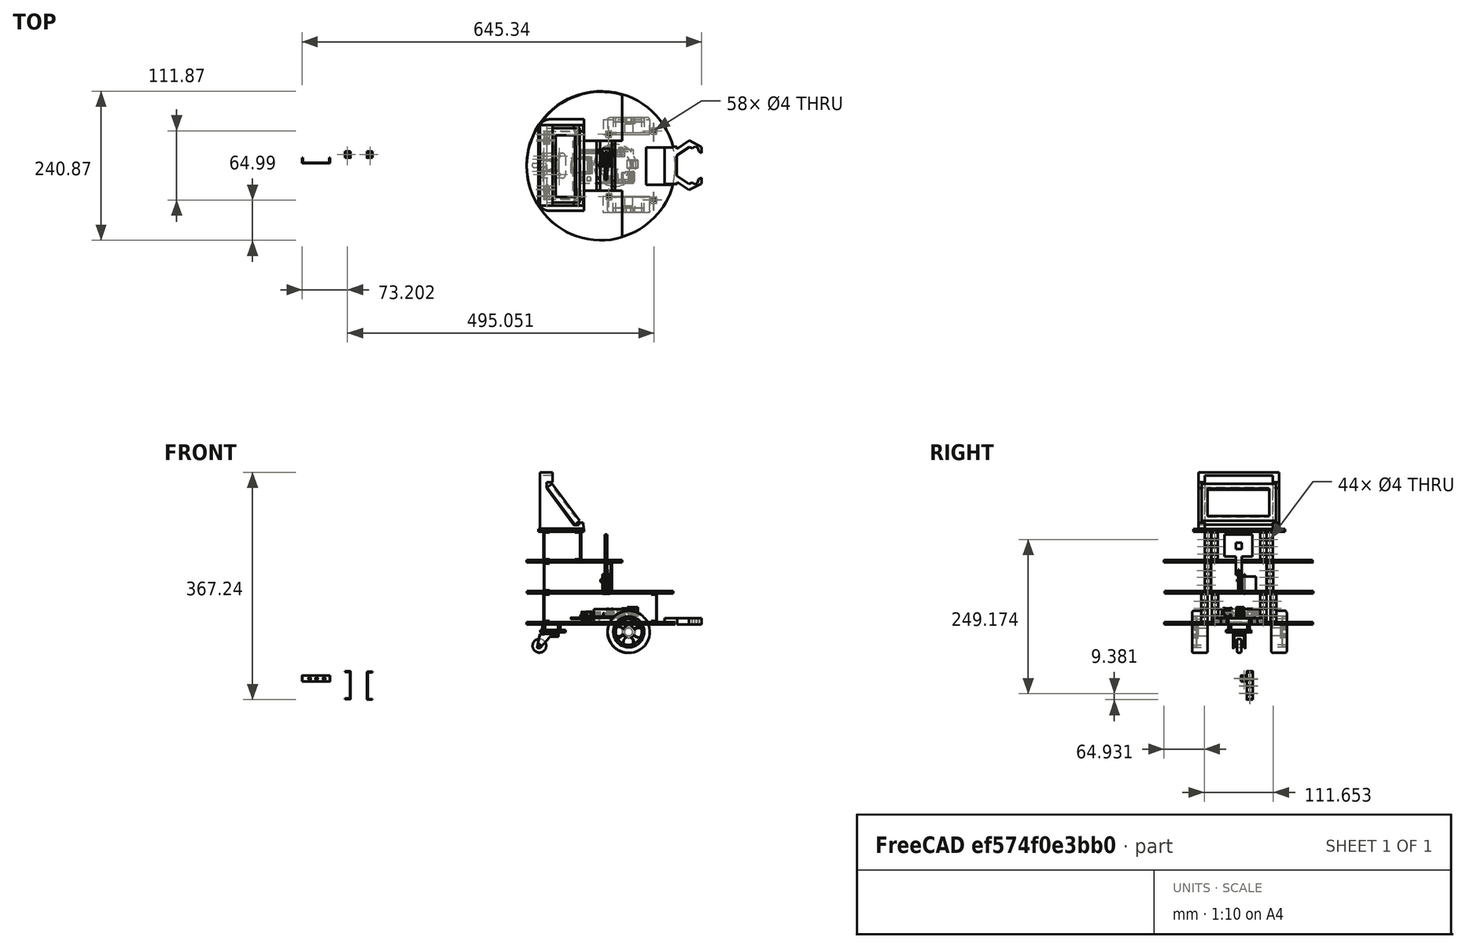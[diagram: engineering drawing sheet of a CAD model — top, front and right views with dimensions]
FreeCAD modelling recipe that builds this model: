
FCSTD DOCUMENT
Label: robot
objects: Part::Feature×53, Part::Cylinder×29, Part::Cut×29, Sketcher::SketchObject×12, PartDesign::Pad×11, App::DocumentObjectGroup×11, Part::MultiFuse×7, Part::Box×7, Part::Fillet×3, Mesh::Feature×1
note: 162 computed .brp shape members not serialized (recipe doc carries the construction recipe); baked Part::Feature solids carry a one-line shape summary decoded from their .brp

FEATURE [Sketcher::SketchObject] Sketch
  sketch-geometry (25):
    g0: LineSegment StartX=6.49 StartY=27.5 StartZ=0 EndX=26.49 EndY=27.5 EndZ=0
    g1: LineSegment StartX=26.49 StartY=27.5 StartZ=0 EndX=26.49 EndY=22.5 EndZ=0
    g2: LineSegment StartX=6.49 StartY=22.5 StartZ=0 EndX=6.49 EndY=27.5 EndZ=0
    g3: Circle CenterX=-114.698 CenterY=15.0203 CenterZ=0 NormalX=0 NormalY=0 NormalZ=1 Radius=2
    g4: Circle CenterX=-114.727 CenterY=-14.9797 CenterZ=0 NormalX=0 NormalY=0 NormalZ=1 Radius=2
    g5: Circle CenterX=-89.6981 CenterY=14.9764 CenterZ=0 NormalX=0 NormalY=0 NormalZ=1 Radius=2
    g6: Circle CenterX=-89.7274 CenterY=-14.9847 CenterZ=0 NormalX=0 NormalY=0 NormalZ=1 Radius=2
    g7: Circle CenterX=-109.963 CenterY=-38.9599 CenterZ=0 NormalX=0 NormalY=0 NormalZ=1 Radius=2
    g8: Circle CenterX=-109.887 CenterY=38.9911 CenterZ=0 NormalX=0 NormalY=0 NormalZ=1 Radius=2
    g9: Circle CenterX=61.9576 CenterY=55.4728 CenterZ=0 NormalX=0 NormalY=0 NormalZ=1 Radius=2
    g10: Circle CenterX=61.8489 CenterY=-55.7773 CenterZ=0 NormalX=0 NormalY=0 NormalZ=1 Radius=2
    g11: LineSegment StartX=56.3229 StartY=50 StartZ=0 EndX=56.3229 EndY=73.8727 EndZ=0
    g12: Circle CenterX=-22.6039 CenterY=-0.518752 CenterZ=0 NormalX=0 NormalY=0 NormalZ=1 Radius=120.029
    g13: LineSegment StartX=-18.6122 StartY=73.8727 StartZ=0 EndX=-18.6122 EndY=50 EndZ=0
    g14: LineSegment StartX=-19.3379 StartY=-50 StartZ=0 EndX=-19.3379 EndY=-75.8206 EndZ=0
    g15: LineSegment StartX=-18.6122 StartY=50 StartZ=0 EndX=56.3229 EndY=50 EndZ=0
    g16: LineSegment StartX=-19.3379 StartY=-50 StartZ=0 EndX=56.3229 EndY=-50 EndZ=0
    g17: LineSegment StartX=56.3229 StartY=-50 StartZ=0 EndX=56.2415 EndY=-75.8206 EndZ=0
    g18: LineSegment StartX=6.49001 StartY=-27.3051 StartZ=0 EndX=27.2747 EndY=-27.3051 EndZ=0
    g19: LineSegment StartX=27.2747 StartY=-27.3051 StartZ=0 EndX=27.2747 EndY=-22.4338 EndZ=0
    g20: LineSegment StartX=6.49001 StartY=-27.3051 StartZ=0 EndX=6.49001 EndY=-22.4338 EndZ=0
    g21: LineSegment StartX=6.49001 StartY=-22.4338 StartZ=0 EndX=27.2747 EndY=-22.4338 EndZ=0
    g22: LineSegment StartX=6.49 StartY=22.5 StartZ=0 EndX=26.49 EndY=22.5 EndZ=0
    g23: LineSegment StartX=-18.6122 StartY=73.8727 StartZ=0 EndX=56.3229 EndY=73.8727 EndZ=0
    g24: LineSegment StartX=-19.3379 StartY=-75.8206 StartZ=0 EndX=56.2415 EndY=-75.8206 EndZ=0
  constraints (25):
    c: Coincident(g0,g1)
    c: Coincident(g2,g0)
    c: Symmetric(g10,g9,g3)
    c: Coincident(g15,g13)
    c: Coincident(g15,g11)
    c: Coincident(g16,g14)
    c: Coincident(g17,g16)
    c: Horizontal(g18)
    c: Coincident(g19,g18)
    c: Vertical(g19)
    c: Coincident(g20,g18)
    c: Vertical(g20)
    c: Coincident(g21,g20)
    c: Coincident(g21,g19)
    c: Horizontal(g21)
    c: Coincident(g22,g2)
    c: Coincident(g22,g1)
    c: Horizontal(g22)
    c: Coincident(g23,g13)
    c: Coincident(g23,g11)
    c: Horizontal(g23)
    c: Coincident(g24,g14)
    c: Coincident(g24,g17)
    c: Horizontal(g24)
    c: Vertical(g14)
FEATURE [Sketcher::SketchObject] Sketch001
  sketch-geometry (25):
    g0: LineSegment [constr] StartX=-124.152 StartY=0.737365 StartZ=0 EndX=-29.7416 EndY=-0.0108822 EndZ=0
    g1: Circle CenterX=-110.299 CenterY=39.0839 CenterZ=0 NormalX=0 NormalY=0 NormalZ=1 Radius=2
    g2: Circle CenterX=-109.764 CenterY=-33.224 CenterZ=0 NormalX=0 NormalY=0 NormalZ=1 Radius=2
    g3: Circle CenterX=62.7977 CenterY=55.4219 CenterZ=0 NormalX=0 NormalY=0 NormalZ=1 Radius=2
    g4: Circle CenterX=62.9826 CenterY=-55.9466 CenterZ=0 NormalX=0 NormalY=0 NormalZ=1 Radius=2
    g5: LineSegment StartX=77.3278 StartY=28.8309 StartZ=0 EndX=50.3934 EndY=28.8309 EndZ=0
    g6: LineSegment StartX=50.3934 StartY=28.8309 StartZ=0 EndX=50.3934 EndY=-31.224 EndZ=0
    g7: Circle CenterX=-110.405 CenterY=-49.217 CenterZ=0 NormalX=0 NormalY=0 NormalZ=1 Radius=2
    g8: Circle CenterX=-109.615 CenterY=50.4676 CenterZ=0 NormalX=0 NormalY=0 NormalZ=1 Radius=2
    g9: Circle CenterX=-10.1147 CenterY=50.2419 CenterZ=0 NormalX=0 NormalY=0 NormalZ=1 Radius=2
    g10: Circle CenterX=-10.1344 CenterY=-50.6043 CenterZ=0 NormalX=0 NormalY=0 NormalZ=1 Radius=2
    g11: LineSegment StartX=-29.7491 StartY=40.2702 StartZ=0 EndX=-23.9444 EndY=40.2702 EndZ=0
    g12: LineSegment StartX=-23.9444 StartY=40.2702 StartZ=0 EndX=-23.9444 EndY=-40.2702 EndZ=0
    g13: LineSegment StartX=-23.9444 StartY=-40.2702 StartZ=0 EndX=-29.7491 EndY=-40.2702 EndZ=0
    g14: LineSegment StartX=-29.7491 StartY=-40.2702 StartZ=0 EndX=-29.7491 EndY=40.2702 EndZ=0
    g15: LineSegment StartX=-5.12768 StartY=40.2702 StartZ=0 EndX=0.362807 EndY=40.2702 EndZ=0
    g16: LineSegment StartX=0.362807 StartY=40.2702 StartZ=0 EndX=0.362807 EndY=-40.2701 EndZ=0
    g17: LineSegment StartX=0.362807 StartY=-40.2701 StartZ=0 EndX=-5.0695 EndY=-40.2701 EndZ=0
    g18: LineSegment StartX=-5.0695 StartY=-40.2701 StartZ=0 EndX=-5.12768 EndY=40.2702 EndZ=0
    g19: LineSegment [constr] StartX=-21.6534 StartY=-0.0749855 StartZ=0 EndX=-5.09844 EndY=-0.206192 EndZ=0
    g20: LineSegment [constr] StartX=50.3934 StartY=-0.645993 StartZ=0 EndX=76.3848 EndY=-0.851987 EndZ=0
    g21: LineSegment StartX=78.2127 StartY=-31.224 StartZ=0 EndX=50.3934 EndY=-31.224 EndZ=0
    g22: ArcOfCircle CenterX=-22.1678 CenterY=-0.347577 CenterZ=0 NormalX=0 NormalY=0 NormalZ=1 Radius=120 StartAngle=0.245617 EndAngle=6.02295
    g23: LineSegment StartX=77.3278 StartY=28.8309 StartZ=0 EndX=94.2307 EndY=28.8309 EndZ=0
    g24: LineSegment StartX=78.2127 StartY=-31.224 StartZ=0 EndX=93.7919 EndY=-31.224 EndZ=0
  constraints (36):
    c: Equal(g2,g1)
    c: Equal(g1,g3)
    c: Equal(g3,g4)
    c: Radius(g2) = 2
    c: Horizontal(g5)
    c: Coincident(g5,g6)
    c: Vertical(g6)
    c: Equal(g7,g8)
    c: Radius(g7) = 2
    c: Radius(g9) = 2
    c: Coincident(g11,g12)
    c: Coincident(g12,g13)
    c: Coincident(g13,g14)
    c: Coincident(g14,g11)
    c: Horizontal(g11)
    c: Horizontal(g13)
    c: Coincident(g15,g16)
    c: Coincident(g16,g17)
    c: Coincident(g17,g18)
    c: Coincident(g18,g15)
    c: Horizontal(g15)
    c: Horizontal(g17)
    c: Symmetric(g7,g8,g3)
    c: Tangent(g0,g19)
    c: PointOnObject(g20,g6)
    c: Tangent(g19,g20)
    c: PointOnObject(g19,g18)
    c: Coincident(g21,g6)
    c: Horizontal(g21)
    c: Radius(g22) = 120
    c: Coincident(g23,g5)
    c: Horizontal(g23)
    c: Horizontal(g24)
    c: Tangent(g24,g2)
    c: Coincident(g22,g23)
    c: Coincident(g22,g24)
FEATURE [PartDesign::Pad] Pad001
  Length = 4
  MirroredExtent = false
  Placement = pos=(0,0,50) rot=(0,0,1;0rad)
  Sketch = -> Sketch001
FEATURE [Sketcher::SketchObject] Sketch002
  sketch-geometry (14):
    g0: Circle CenterX=-109.932 CenterY=49.3917 CenterZ=0 NormalX=0 NormalY=0 NormalZ=1 Radius=2
    g1: Circle CenterX=-110.012 CenterY=-50.1232 CenterZ=0 NormalX=0 NormalY=0 NormalZ=1 Radius=2
    g2: Circle CenterX=-9.94777 CenterY=50.1271 CenterZ=0 NormalX=0 NormalY=0 NormalZ=1 Radius=2
    g3: Circle CenterX=-10.198 CenterY=-50.2781 CenterZ=0 NormalX=0 NormalY=0 NormalZ=1 Radius=2
    g4: LineSegment StartX=-67.9878 StartY=-40.9294 StartZ=0 EndX=-67.9878 EndY=39.6614 EndZ=0
    g5: Circle CenterX=-109.839 CenterY=41.6614 CenterZ=0 NormalX=0 NormalY=0 NormalZ=1 Radius=2
    g6: Circle CenterX=-110.415 CenterY=-38.9294 CenterZ=0 NormalX=0 NormalY=0 NormalZ=1 Radius=2
    g7: Circle CenterX=-59.5193 CenterY=-50.2572 CenterZ=0 NormalX=0 NormalY=0 NormalZ=1 Radius=2
    g8: Circle CenterX=-60.2629 CenterY=49.9665 CenterZ=0 NormalX=0 NormalY=0 NormalZ=1 Radius=2
    g9: ArcOfCircle CenterX=-22.4312 CenterY=-1.22279 CenterZ=0 NormalX=0 NormalY=0 NormalZ=1 Radius=120 StartAngle=1.28265 EndAngle=5.00053
    g10: LineSegment StartX=11.6694 StartY=113.83 StartZ=0 EndX=11.6694 EndY=39.6614 EndZ=0
    g11: LineSegment StartX=-67.9878 StartY=39.6614 StartZ=0 EndX=11.6694 EndY=39.6614 EndZ=0
    g12: LineSegment StartX=-67.9878 StartY=-40.9294 StartZ=0 EndX=11.6694 EndY=-40.9294 EndZ=0
    g13: LineSegment StartX=11.6694 StartY=-40.9294 StartZ=0 EndX=11.6694 EndY=-116.276 EndZ=0
  constraints (22):
    c: Equal(g0,g1)
    c: Equal(g1,g3)
    c: Equal(g3,g2)
    c: Radius(g0) = 2
    c: Vertical(g4)
    c: Equal(g6,g5)
    c: Equal(g5,g8)
    c: Equal(g8,g7)
    c: Radius(g6) = 2
    c: Radius(g9) = 120
    c: Vertical(g10)
    c: Coincident(g9,g10)
    c: Coincident(g9,g13)
    c: Coincident(g11,g4)
    c: Horizontal(g11)
    c: Tangent(g11,g5)
    c: Coincident(g12,g4)
    c: Horizontal(g12)
    c: Tangent(g12,g6)
    c: Coincident(g10,g11)
    c: Coincident(g13,g12)
    c: Tangent(g10,g13)
FEATURE [PartDesign::Pad] Pad002
  Length = 4
  MirroredExtent = false
  Placement = pos=(0,0,100) rot=(0,0,1;0rad)
  Sketch = -> Sketch002
FEATURE [Sketcher::SketchObject] Sketch003
  sketch-geometry (12):
    g0: ArcOfCircle CenterX=-105.074 CenterY=55.6821 CenterZ=0 NormalX=0 NormalY=0 NormalZ=1 Radius=18.6332 StartAngle=1.60655 EndAngle=3.14159
    g1: ArcOfCircle CenterX=-105.346 CenterY=-55.3418 CenterZ=0 NormalX=0 NormalY=0 NormalZ=1 Radius=18.3958 StartAngle=3.20271 EndAngle=4.69093
    g2: LineSegment StartX=-50.0043 StartY=74.3033 StartZ=0 EndX=-50.0043 EndY=-73.7333 EndZ=0
    g3: LineSegment StartX=-105.74 StartY=74.3033 StartZ=0 EndX=-50.0043 EndY=74.3033 EndZ=0
    g4: LineSegment StartX=-105.741 StartY=-73.7333 StartZ=0 EndX=-50.0043 EndY=-73.7333 EndZ=0
    g5: Circle CenterX=-109.743 CenterY=39.5908 CenterZ=0 NormalX=0 NormalY=0 NormalZ=1 Radius=2
    g6: Circle CenterX=-110.279 CenterY=-40.0459 CenterZ=0 NormalX=0 NormalY=0 NormalZ=1 Radius=2
    g7: Circle CenterX=-60.203 CenterY=49.9128 CenterZ=0 NormalX=0 NormalY=0 NormalZ=1 Radius=2
    g8: Circle CenterX=-59.3002 CenterY=-50.3702 CenterZ=0 NormalX=0 NormalY=0 NormalZ=1 Radius=2
    g9: Circle CenterX=-116.132 CenterY=9.74953 CenterZ=0 NormalX=0 NormalY=0 NormalZ=1 Radius=2
    g10: Circle CenterX=-116.544 CenterY=-9.66085 CenterZ=0 NormalX=0 NormalY=0 NormalZ=1 Radius=2
    g11: LineSegment StartX=-123.707 StartY=55.6821 StartZ=0 EndX=-123.707 EndY=-56.4655 EndZ=0
  constraints (17):
    c: Coincident(g3,g0)
    c: Coincident(g3,g2)
    c: Coincident(g4,g1)
    c: Coincident(g4,g2)
    c: Equal(g6,g5)
    c: Equal(g5,g7)
    c: Equal(g7,g8)
    c: Radius(g6) = 2
    c: Horizontal(g3)
    c: Vertical(g2)
    c: Horizontal(g4)
    c: Equal(g10,g9)
    c: Radius(g9) = 2
    c: Coincident(g11,g0)
    c: Coincident(g11,g1)
    c: Vertical(g11)
    c: Tangent(g11,g0)
FEATURE [PartDesign::Pad] Pad003
  Length = 4
  MirroredExtent = false
  Placement = pos=(0,0,150) rot=(0,0,1;0rad)
  Sketch = -> Sketch003
FEATURE [Part::Cylinder] Cylinder005
  Angle = 360
  Height = 25
  Radius = 6.5
FEATURE [Part::Cylinder] Cylinder006
  Angle = 360
  Height = 10
  Radius = 10
FEATURE [Part::Cylinder] Cylinder010
  Angle = 360
  Height = 7
  Placement = pos=(0.664718,-16.3626,0) rot=(0,0,1;0rad)
  Radius = 8
FEATURE [Part::Cylinder] Cylinder011
  Angle = 360
  Height = 7
  Placement = pos=(16.4955,0.685902,0) rot=(0,0,1;0rad)
  Radius = 8
FEATURE [Part::Cylinder] Cylinder012
  Angle = 360
  Height = 7
  Placement = pos=(-16.3838,-1.44516,0) rot=(0,0,1;0rad)
  Radius = 8
FEATURE [Part::Cylinder] Cylinder013
  Angle = 360
  Height = 25
  Radius = 25
FEATURE [Part::Cylinder] Cylinder009
  Angle = 360
  Height = 7
  Placement = pos=(-0.248596,16.2122,0) rot=(0,0,1;0rad)
  Radius = 8
FEATURE [Part::MultiFuse] Fusion
  Placement = pos=(22,77,-12) rot=(1,0,0;1.5708rad)
  Shapes = -> [Cylinder006,Cylinder011,Cylinder012,Cylinder010,Cylinder009,Cylinder005]
FEATURE [Part::Cylinder] Cylinder014
  Angle = 360
  Height = 25
  Radius = 34
FEATURE [Part::Cylinder] Cylinder015
  Angle = 360
  Height = 25
  Radius = 21
FEATURE [Part::Cylinder] Cylinder016
  Angle = 360
  Height = 25
  Radius = 25
FEATURE [Part::Cut] Cut002
  Base = -> Cylinder016
  Placement = pos=(22,77,-12) rot=(1,0,0;1.5708rad)
  Tool = -> Cylinder015
FEATURE [Part::Fillet] Fillet
  Edges = 2 edges r=3: [Edge2,Edge3]
  Placement = pos=(22,77,-12) rot=(1,0,0;1.5708rad)
FEATURE [App::DocumentObjectGroup] Group  label="wheel"
  Group = -> [Cut002,Fusion,Fillet]
FEATURE [Part::Cylinder] Cylinder
  Angle = 360
  Height = 7
  Radius = 11
FEATURE [Part::Cylinder] Cylinder017
  Angle = 360
  Height = 7
  Radius = 2.5
FEATURE [Part::Cut] Cut
  Base = -> Cylinder
  Tool = -> Cylinder017
FEATURE [Part::Fillet] Fillet001
  Base = -> Cut
  Edges = 4 edges r=2: [Edge1,Edge3,Edge4,Edge5]
  Placement = pos=(-122,-3.4,-34.5) rot=(0,0.707107,0.707107;3.14159rad)
FEATURE [App::DocumentObjectGroup] Group001  label="wheel0"
  Group = -> [Cylinder017,Cylinder,Fillet001]
FEATURE [Sketcher::SketchObject] Sketch004
  sketch-geometry (11):
    g0: LineSegment StartX=-39.5249 StartY=-0.0489382 StartZ=0 EndX=-9.52487 EndY=-0.0489382 EndZ=0
    g1: LineSegment StartX=-9.52487 StartY=-0.0489382 StartZ=0 EndX=-5.3256 EndY=-21.3647 EndZ=0
    g2: LineSegment StartX=-6.46484 StartY=-22.7502 StartZ=0 EndX=-9.08519 EndY=-22.7502 EndZ=0
    g3: LineSegment StartX=-10.2117 StartY=-22.2424 StartZ=0 EndX=-25.3922 EndY=-5.06478 EndZ=0
    g4: LineSegment StartX=-27.2038 StartY=-4.24812 StartZ=0 EndX=-38.567 EndY=-4.24812 EndZ=0
    g5: LineSegment StartX=-39.5249 StartY=-3.29027 StartZ=0 EndX=-39.5249 EndY=-0.0489382 EndZ=0
    g6: ArcOfCircle CenterX=-6.46484 CenterY=-21.5891 CenterZ=0 NormalX=0 NormalY=0 NormalZ=1 Radius=1.16114 StartAngle=4.71239 EndAngle=6.4777
    g7: ArcOfCircle CenterX=-9.08519 CenterY=-21.2469 CenterZ=0 NormalX=0 NormalY=0 NormalZ=1 Radius=1.50333 StartAngle=3.86535 EndAngle=4.71239
    g8: ArcOfCircle CenterX=-27.2038 CenterY=-6.66574 CenterZ=0 NormalX=0 NormalY=0 NormalZ=1 Radius=2.41762 StartAngle=0.723759 EndAngle=1.5708
    g9: Circle CenterX=-8.87657 CenterY=-18.7194 CenterZ=0 NormalX=0 NormalY=0 NormalZ=1 Radius=2
    g10: ArcOfCircle CenterX=-38.567 CenterY=-3.29027 CenterZ=0 NormalX=0 NormalY=0 NormalZ=1 Radius=0.95785 StartAngle=3.14159 EndAngle=4.71239
  constraints (16):
    c: Horizontal(g0)
    c: Distance(g0) = 30
    c: Coincident(g1,g0)
    c: Horizontal(g2)
    c: Horizontal(g4)
    c: Coincident(g5,g0)
    c: Vertical(g5)
    c: Tangent(g1,g6)
    c: Tangent(g2,g6)
    c: Tangent(g2,g7)
    c: Tangent(g3,g7)
    c: Tangent(g3,g8)
    c: Tangent(g4,g8)
    c: Radius(g9) = 2
    c: Tangent(g4,g10)
    c: Tangent(g5,g10)
FEATURE [PartDesign::Pad] Pad004
  Length = 20
  MirroredExtent = false
  Placement = pos=(40,27,-2) rot=(0,0,1;0rad)
  Sketch = -> Sketch004
FEATURE [Part::Box] Box
  Height = 16
  Length = 40
  Width = 25
FEATURE [Part::Cut] Cut003
  Base = -> Pad004
  Placement = pos=(-90.7,-8,-42.5) rot=(0,0.707107,0.707107;3.14159rad)
  Tool = -> Box
FEATURE [App::DocumentObjectGroup] Group002  label="wl"
  Group = -> [Cut003]
FEATURE [Part::Fillet] Fillet002
  Edges = 2 edges r=3: [Edge2,Edge3]
  Placement = pos=(22.3,-76,-12) rot=(0,0.707107,0.707107;3.14159rad)
FEATURE [Part::MultiFuse] Fusion001
  Placement = pos=(22.3,-76,-12) rot=(0,0.707107,0.707107;3.14159rad)
  Shapes = -> [Cylinder006,Cylinder011,Cylinder012,Cylinder010,Cylinder009,Cylinder005]
FEATURE [Part::Cut] Cut004
  Base = -> Cylinder016
  Placement = pos=(22.3,-76,-12) rot=(0,0.707107,0.707107;3.14159rad)
  Tool = -> Cylinder015
FEATURE [App::DocumentObjectGroup] Group003  label="wheel01"
  Group = -> [Cut004,Fusion001,Fillet002]
FEATURE [App::DocumentObjectGroup] Group004
FEATURE [Sketcher::SketchObject] Sketch005  label="Sketch_plate"
  sketch-geometry (12):
    g0: LineSegment StartX=-114.888 StartY=19.7983 StartZ=0 EndX=-85.6217 EndY=19.7983 EndZ=0
    g1: LineSegment StartX=-80.1008 StartY=14.2774 StartZ=0 EndX=-80.1008 EndY=-15.4701 EndZ=0
    g2: LineSegment StartX=-85.6217 StartY=-20.991 StartZ=0 EndX=-114.888 EndY=-20.991 EndZ=0
    g3: LineSegment StartX=-120.409 StartY=-15.4701 StartZ=0 EndX=-120.409 EndY=14.2774 EndZ=0
    g4: Circle CenterX=-115.076 CenterY=14.931 CenterZ=0 NormalX=0 NormalY=0 NormalZ=1 Radius=2
    g5: Circle CenterX=-115.258 CenterY=-14.9052 CenterZ=0 NormalX=0 NormalY=0 NormalZ=1 Radius=2
    g6: Circle CenterX=-90.0087 CenterY=14.931 CenterZ=0 NormalX=0 NormalY=0 NormalZ=1 Radius=2
    g7: Circle CenterX=-89.8897 CenterY=-14.9413 CenterZ=0 NormalX=0 NormalY=0 NormalZ=1 Radius=2
    g8: ArcOfCircle CenterX=-85.6217 CenterY=14.2774 CenterZ=0 NormalX=0 NormalY=0 NormalZ=1 Radius=5.52093 StartAngle=0 EndAngle=1.5708
    g9: ArcOfCircle CenterX=-85.6217 CenterY=-15.4701 CenterZ=0 NormalX=0 NormalY=0 NormalZ=1 Radius=5.52093 StartAngle=4.71239 EndAngle=6.28319
    g10: ArcOfCircle CenterX=-114.888 CenterY=14.2774 CenterZ=0 NormalX=0 NormalY=0 NormalZ=1 Radius=5.52093 StartAngle=1.5708 EndAngle=3.14159
    g11: ArcOfCircle CenterX=-114.888 CenterY=-15.4701 CenterZ=0 NormalX=0 NormalY=0 NormalZ=1 Radius=5.52093 StartAngle=3.14159 EndAngle=4.71239
  constraints (19):
    c: Horizontal(g0)
    c: Horizontal(g2)
    c: Vertical(g1)
    c: Vertical(g3)
    c: Equal(g4,g5)
    c: Equal(g5,g7)
    c: Equal(g7,g6)
    c: Radius(g6) = 2
    c: Tangent(g0,g8)
    c: Tangent(g1,g8)
    c: Tangent(g1,g9)
    c: Tangent(g2,g9)
    c: Tangent(g0,g10)
    c: Tangent(g3,g10)
    c: Tangent(g2,g11)
    c: Tangent(g3,g11)
    c: Equal(g11,g10)
    c: Equal(g10,g8)
    c: Equal(g8,g9)
FEATURE [PartDesign::Pad] Pad
  Length = 4
  MirroredExtent = false
  Sketch = -> Sketch
FEATURE [PartDesign::Pad] Pad005
  Length = 4
  MirroredExtent = false
  Placement = pos=(0,0,-13) rot=(0,0,1;0rad)
  Sketch = -> Sketch005
FEATURE [Part::Cylinder] Cylinder018
  Angle = 360
  Height = 4
  Placement = pos=(-107,0,-16) rot=(0,0,1;0rad)
  Radius = 7
FEATURE [Part::Cylinder] Cylinder019
  Angle = 360
  Height = 10
  Placement = pos=(-115.055,-14.9752,-9) rot=(0,0,1;0rad)
  Radius = 2
FEATURE [Part::Cylinder] Cylinder020
  Angle = 360
  Height = 10
  Placement = pos=(-90.0431,-15,-10) rot=(0,0,1;0rad)
  Radius = 2
FEATURE [Part::Cylinder] Cylinder021
  Angle = 360
  Height = 10
  Placement = pos=(-89.9511,14.932,-10) rot=(0,0,1;0rad)
  Radius = 2
FEATURE [Part::Cylinder] Cylinder022
  Angle = 360
  Height = 10
  Placement = pos=(-115.109,14.8885,-9) rot=(0,0,1;0rad)
  Radius = 2
FEATURE [Sketcher::SketchObject] Sketch006
  sketch-geometry (15):
    g0: LineSegment StartX=-29.9116 StartY=5.05926 StartZ=0 EndX=30.0884 EndY=5.05926 EndZ=0
    g1: LineSegment StartX=34.7894 StartY=0.358325 StartZ=0 EndX=34.7894 EndY=-0.239814 EndZ=0
    g2: LineSegment StartX=30.0884 StartY=-4.94074 StartZ=0 EndX=-29.9116 EndY=-4.94074 EndZ=0
    g3: LineSegment StartX=-34.6125 StartY=-0.239814 StartZ=0 EndX=-34.6125 EndY=0.358325 EndZ=0
    g4: ArcOfCircle CenterX=-29.9116 CenterY=0.358325 CenterZ=0 NormalX=0 NormalY=0 NormalZ=1 Radius=4.70093 StartAngle=1.5708 EndAngle=3.14159
    g5: ArcOfCircle CenterX=-29.9116 CenterY=-0.239814 CenterZ=0 NormalX=0 NormalY=0 NormalZ=1 Radius=4.70093 StartAngle=3.14159 EndAngle=4.71239
    g6: ArcOfCircle CenterX=30.0884 CenterY=0.358325 CenterZ=0 NormalX=0 NormalY=0 NormalZ=1 Radius=4.70093 StartAngle=0 EndAngle=1.5708
    g7: ArcOfCircle CenterX=30.0884 CenterY=-0.239814 CenterZ=0 NormalX=0 NormalY=0 NormalZ=1 Radius=4.70093 StartAngle=4.71239 EndAngle=6.28319
    g8: Circle CenterX=-29.9299 CenterY=0.0119776 CenterZ=0 NormalX=0 NormalY=0 NormalZ=1 Radius=2
    g9: Circle CenterX=-11.1706 CenterY=0.0385086 CenterZ=0 NormalX=0 NormalY=0 NormalZ=1 Radius=2
    g10: Circle CenterX=11.1127 CenterY=-0.0115485 CenterZ=0 NormalX=0 NormalY=0 NormalZ=1 Radius=2
    g11: Circle CenterX=0.0455946 CenterY=-0.112972 CenterZ=0 NormalX=0 NormalY=0 NormalZ=1 Radius=2
    g12: Circle CenterX=30.0576 CenterY=0.117842 CenterZ=0 NormalX=0 NormalY=0 NormalZ=1 Radius=2
    g13: LineSegment StartX=25.3875 StartY=-4.94074 StartZ=0 EndX=25.3875 EndY=5.05926 EndZ=0
    g14: LineSegment StartX=-25.2106 StartY=-4.94074 StartZ=0 EndX=-25.2106 EndY=5.05926 EndZ=0
  constraints (30):
    c: Horizontal(g0)
    c: Horizontal(g2)
    c: Vertical(g1)
    c: Vertical(g3)
    c: Tangent(g0,g4)
    c: Tangent(g3,g4)
    c: Tangent(g2,g5)
    c: Tangent(g3,g5)
    c: Tangent(g0,g6)
    c: Tangent(g1,g6)
    c: Tangent(g1,g7)
    c: Tangent(g2,g7)
    c: Equal(g4,g5)
    c: Equal(g5,g6)
    c: Equal(g6,g7)
    c: Distance(g2) = 60
    c: DistanceY(g0,g2) = -10
    c: Equal(g8,g9)
    c: Equal(g9,g10)
    c: Equal(g10,g11)
    c: Equal(g11,g12)
    c: Radius(g8) = 2
    c: PointOnObject(g13,g2)
    c: PointOnObject(g13,g0)
    c: Vertical(g13)
    c: Tangent(g13,g6)
    c: PointOnObject(g14,g2)
    c: PointOnObject(g14,g0)
    c: Vertical(g14)
    c: Tangent(g14,g4)
FEATURE [Sketcher::SketchObject] Sketch007
  sketch-geometry (12):
    g0: LineSegment StartX=20.5461 StartY=-1.20827 StartZ=0 EndX=-22.4155 EndY=-1.20827 EndZ=0
    g1: LineSegment StartX=-23.4007 StartY=7.77698 StartZ=0 EndX=-22.4007 EndY=7.77698 EndZ=0
    g2: LineSegment StartX=-22.4007 StartY=7.77698 StartZ=0 EndX=-22.4007 EndY=0.197829 EndZ=0
    g3: LineSegment StartX=21.5992 StartY=7.84487 StartZ=0 EndX=20.5992 EndY=7.84487 EndZ=0
    g4: LineSegment StartX=20.5992 StartY=7.84487 StartZ=0 EndX=20.5992 EndY=-0.149263 EndZ=0
    g5: LineSegment StartX=-22.0096 StartY=-0.193299 StartZ=0 EndX=20.5552 EndY=-0.193299 EndZ=0
    g6: LineSegment StartX=-23.4007 StartY=7.77698 StartZ=0 EndX=-23.4007 EndY=-0.223018 EndZ=0
    g7: LineSegment StartX=21.5992 StartY=7.84487 StartZ=0 EndX=21.5992 EndY=-0.155135 EndZ=0
    g8: ArcOfCircle CenterX=-22.4155 CenterY=-0.223018 CenterZ=0 NormalX=0 NormalY=0 NormalZ=1 Radius=0.985254 StartAngle=3.14159 EndAngle=4.71239
    g9: ArcOfCircle CenterX=20.5461 CenterY=-0.155135 CenterZ=0 NormalX=0 NormalY=0 NormalZ=1 Radius=1.05314 StartAngle=4.71239 EndAngle=6.28319
    g10: ArcOfCircle CenterX=20.5552 CenterY=-0.149263 CenterZ=0 NormalX=0 NormalY=0 NormalZ=1 Radius=0.044036 StartAngle=4.71239 EndAngle=6.28319
    g11: ArcOfCircle CenterX=-22.0096 CenterY=0.197829 CenterZ=0 NormalX=0 NormalY=0 NormalZ=1 Radius=0.391129 StartAngle=3.14159 EndAngle=4.71239
  constraints (25):
    c: Coincident(g2,g1)
    c: Vertical(g2)
    c: Coincident(g4,g3)
    c: Vertical(g4)
    c: Distance(g1) = 1
    c: Distance(g3) = 1
    c: Coincident(g6,g1)
    c: Vertical(g6)
    c: Coincident(g7,g3)
    c: Vertical(g7)
    c: Tangent(g0,g8)
    c: Tangent(g6,g8)
    c: Tangent(g0,g9)
    c: Tangent(g7,g9)
    c: Tangent(g4,g10)
    c: Tangent(g5,g10)
    c: Tangent(g2,g11)
    c: Tangent(g5,g11)
    c: Distance(g1,g3) = 43
    c: Distance(g3,g7) = 8
    c: Distance(g1,g6) = 8
    c: Horizontal(g5)
    c: Horizontal(g0)
    c: Horizontal(g1)
    c: Horizontal(g3)
FEATURE [PartDesign::Pad] Pad006
  Length = 10
  MirroredExtent = false
  Sketch = -> Sketch007
FEATURE [Part::Cylinder] Cylinder025
  Angle = 360
  Height = 2
  Placement = pos=(25,5.38,4.9) rot=(0.706319,-0.023027,0.707519;3.16911rad)
  Radius = 2
FEATURE [Part::Cylinder] Cylinder026
  Angle = 360
  Height = 2
  Placement = pos=(-26,5.29,4.9) rot=(0.706319,-0.023027,0.707519;3.16911rad)
  Radius = 2
FEATURE [Part::Cylinder] Cylinder027
  Angle = 360
  Height = 2
  Placement = pos=(12.2129,0,4.81114) rot=(1,0,0;1.5708rad)
  Radius = 2
FEATURE [Part::Cylinder] Cylinder028
  Angle = 360
  Height = 2
  Placement = pos=(-11.1555,-4.76837e-07,4.86401) rot=(1,0,0;1.5708rad)
  Radius = 2
FEATURE [Part::Cylinder] Cylinder029
  Angle = 360
  Height = 2
  Placement = pos=(-2.98023e-07,0,4.86401) rot=(1,0,0;1.5708rad)
  Radius = 2
FEATURE [Part::Cut] Cut005
  Base = -> Pad006
  Tool = -> Cylinder025
FEATURE [Part::Cut] Cut006
  Base = -> Cut005
  Tool = -> Cylinder027
FEATURE [Part::Cut] Cut007
  Base = -> Cut006
  Tool = -> Cylinder029
FEATURE [Part::Cut] Cut008
  Base = -> Cut007
  Tool = -> Cylinder028
FEATURE [Part::Cut] Cut009
  Base = -> Cut008
  Tool = -> Cylinder026
FEATURE [Part::MultiFuse] Fusion002  label="back_wheel"
  Shapes = -> [Fillet001,Pad005,Cylinder018,Cylinder019,Cylinder020,Cylinder021,Cylinder022,Cut003]
FEATURE [Part::Cylinder] Cylinder030
  Angle = 360
  Height = 10
  Placement = pos=(15.49,3.9,4.87) rot=(0,1,0;1.5708rad)
  Radius = 2
FEATURE [Part::Cylinder] Cylinder031
  Angle = 360
  Height = 10
  Placement = pos=(-28.4147,3.9,5.14) rot=(0,1,0;1.5708rad)
  Radius = 2
FEATURE [Part::Cut] Cut018
  Base = -> Cut009
  Tool = -> Cylinder031
FEATURE [Part::Cut] Cut019
  Base = -> Cut018
  Placement = pos=(-481.872,4.52656,-92.3721) rot=(0,0,1;0rad)
  Tool = -> Cylinder030
FEATURE [Part::Cut] Cut022
  Base = -> Cut018
  Placement = pos=(-428.168,12.2394,-99.0758) rot=(-0.57735,0.57735,0.57735;2.0944rad)
  Tool = -> Cylinder030
FEATURE [Part::Cut] Cut023
  Base = -> Cut018
  Placement = pos=(-399.312,22.2394,-99.8057) rot=(0.57735,0.57735,-0.57735;2.0944rad)
  Tool = -> Cylinder030
FEATURE [App::DocumentObjectGroup] Group005  label="junk"
  Group = -> [Sketch006,Group001,Group002,Group004,Cut008,Cut019,Cut022,Cut023,Cylinder014,Cylinder013]
FEATURE [Part::Cut] Cut024
  Base = -> Cut018
  Placement = pos=(-114,44,26) rot=(0.57735,0.57735,-0.57735;2.0944rad)
  Tool = -> Cylinder030
FEATURE [Part::Cut] Cut025
  Base = -> Cut018
  Placement = pos=(66.5,-61.1,26) rot=(0.57735,-0.57735,-0.57735;4.18879rad)
  Tool = -> Cylinder030
FEATURE [Part::Cut] Cut026
  Base = -> Cut018
  Placement = pos=(66.5,50.5,26) rot=(0.57735,-0.57735,-0.57735;4.18879rad)
  Tool = -> Cylinder030
FEATURE [Part::Cut] Cut027
  Base = -> Cut018
  Placement = pos=(-113.8,-33.8,26) rot=(0.57735,0.57735,-0.57735;2.0944rad)
  Tool = -> Cylinder030
FEATURE [Part::Cut] Cut028
  Base = -> Cut018
  Placement = pos=(-113.8,54.6,75.9572) rot=(0.57735,0.57735,-0.57735;2.0944rad)
  Tool = -> Cylinder030
FEATURE [Part::Cut] Cut029
  Base = -> Cut018
  Placement = pos=(-113.8,-45.5244,76) rot=(0.57735,0.57735,-0.57735;2.0944rad)
  Tool = -> Cylinder030
FEATURE [Part::Cut] Cut030
  Base = -> Cut018
  Placement = pos=(-6.72542,45.23,76) rot=(0.57735,-0.57735,-0.57735;4.18879rad)
  Tool = -> Cylinder030
FEATURE [Part::Cut] Cut031
  Base = -> Cut018
  Placement = pos=(-6.2,-55.7,76) rot=(0.57735,-0.57735,-0.57735;4.18879rad)
  Tool = -> Cylinder030
FEATURE [Part::Cut] Cut032
  Base = -> Cut018
  Placement = pos=(-56.7371,44.4421,126) rot=(0.57735,-0.57735,-0.57735;4.18879rad)
  Tool = -> Cylinder030
FEATURE [Part::Cut] Cut033
  Base = -> Cut018
  Placement = pos=(-55.7549,-55.4537,126) rot=(0.57735,-0.57735,-0.57735;4.18879rad)
  Tool = -> Cylinder030
FEATURE [Part::Cut] Cut034
  Base = -> Cut018
  Placement = pos=(-114.175,-34.5899,126) rot=(0.57735,0.57735,-0.57735;2.0944rad)
  Tool = -> Cylinder030
FEATURE [Part::Cut] Cut035
  Base = -> Cut018
  Placement = pos=(-113.675,44.2743,126) rot=(0.57735,0.57735,-0.57735;2.0944rad)
  Tool = -> Cylinder030
FEATURE [App::DocumentObjectGroup] Group006  label="flor0"
  Group = -> [Cut027,Cut026,Cut025,Cut024]
FEATURE [App::DocumentObjectGroup] Group007  label="flor1"
  Group = -> [Cut028,Cut029,Cut030,Cut031]
FEATURE [App::DocumentObjectGroup] Group008  label="flor2"
  Group = -> [Cut032,Cut033,Cut034,Cut035]
FEATURE [Sketcher::SketchObject] Sketch008  label="gropper"
  sketch-geometry (24):
    g0: LineSegment StartX=80.2034 StartY=30.1452 StartZ=0 EndX=100.11 EndY=30.1452 EndZ=0
    g1: LineSegment StartX=100.216 StartY=-30.1776 StartZ=0 EndX=80.2034 EndY=-30.1776 EndZ=0
    g2: LineSegment StartX=80.2034 StartY=-30.1776 StartZ=0 EndX=80.2034 EndY=30.1452 EndZ=0
    g3: LineSegment StartX=139.974 StartY=29.5055 StartZ=0 EndX=139.974 EndY=19.9512 EndZ=0
    g4: LineSegment StartX=139.709 StartY=-20.0089 StartZ=0 EndX=140.068 EndY=-29.5025 EndZ=0
    g5: LineSegment StartX=125.379 StartY=27.6382 StartZ=0 EndX=129.678 EndY=30.5041 EndZ=0
    g6: LineSegment StartX=129.678 StartY=30.5041 StartZ=0 EndX=134.515 EndY=27.6382 EndZ=0
    g7: LineSegment StartX=134.515 StartY=27.6382 StartZ=0 EndX=135.589 EndY=22.4435 EndZ=0
    g8: LineSegment StartX=135.589 StartY=22.4435 StartZ=0 EndX=139.974 EndY=19.9512 EndZ=0
    g9: LineSegment StartX=124.663 StartY=-27.7113 StartZ=0 EndX=128.962 EndY=-31.1146 EndZ=0
    g10: LineSegment StartX=128.962 StartY=-31.1146 StartZ=0 EndX=133.619 EndY=-28.4278 EndZ=0
    g11: LineSegment StartX=133.619 StartY=-28.4278 StartZ=0 EndX=135.052 EndY=-22.8749 EndZ=0
    g12: LineSegment StartX=135.052 StartY=-22.8749 StartZ=0 EndX=139.709 EndY=-20.0089 EndZ=0
    g13: LineSegment StartX=100.11 StartY=30.1452 StartZ=0 EndX=100.11 EndY=26.5496 EndZ=0
    g14: LineSegment StartX=100.149 StartY=16.1353 StartZ=0 EndX=100.149 EndY=-17.1102 EndZ=0
    g15: LineSegment StartX=100.216 StartY=-30.1776 StartZ=0 EndX=100.216 EndY=-26.8315 EndZ=0
    g16: LineSegment StartX=100.11 StartY=26.5496 StartZ=0 EndX=120.202 EndY=39.9887 EndZ=0
    g17: LineSegment StartX=120.269 StartY=29.7499 StartZ=0 EndX=100.149 EndY=16.1353 EndZ=0
    g18: LineSegment StartX=119.814 StartY=-30.0538 StartZ=0 EndX=100.149 EndY=-17.1102 EndZ=0
    g19: LineSegment StartX=100.216 StartY=-26.8315 StartZ=0 EndX=119.826 EndY=-39.8917 EndZ=0
    g20: LineSegment StartX=120.202 StartY=39.9887 StartZ=0 EndX=139.974 EndY=29.5055 EndZ=0
    g21: LineSegment StartX=120.269 StartY=29.7499 StartZ=0 EndX=125.379 EndY=27.6382 EndZ=0
    g22: LineSegment StartX=119.814 StartY=-30.0538 StartZ=0 EndX=124.663 EndY=-27.7113 EndZ=0
    g23: LineSegment StartX=119.826 StartY=-39.8917 StartZ=0 EndX=140.068 EndY=-29.5025 EndZ=0
  constraints (30):
    c: Coincident(g1,g2)
    c: Coincident(g2,g0)
    c: Horizontal(g0)
    c: Horizontal(g1)
    c: Vertical(g2)
    c: Coincident(g5,g6)
    c: Coincident(g6,g7)
    c: Coincident(g7,g8)
    c: Coincident(g8,g3)
    c: Coincident(g9,g10)
    c: Coincident(g10,g11)
    c: Coincident(g11,g12)
    c: Coincident(g12,g4)
    c: Coincident(g13,g0)
    c: Vertical(g13)
    c: Vertical(g14)
    c: Coincident(g15,g1)
    c: Vertical(g15)
    c: Coincident(g16,g13)
    c: Coincident(g17,g14)
    c: Coincident(g18,g14)
    c: Coincident(g19,g15)
    c: Coincident(g20,g16)
    c: Coincident(g20,g3)
    c: Coincident(g21,g17)
    c: Coincident(g21,g5)
    c: Coincident(g22,g18)
    c: Coincident(g22,g9)
    c: Coincident(g23,g19)
    c: Coincident(g23,g4)
FEATURE [PartDesign::Pad] Pad007  label="gripper"
  Length = 10
  MirroredExtent = false
  Sketch = -> Sketch008
FEATURE [Part::Box] Box001
  Height = 87
  Length = 80
  Placement = pos=(-50,26,251.5) rot=(0,1,0;3.14159rad)
  Width = 110
FEATURE [Sketcher::SketchObject] Sketch009
  sketch-geometry (11):
    g0: LineSegment StartX=-120.266 StartY=55.8702 StartZ=0 EndX=-120.266 EndY=-35.2585 EndZ=0
    g1: LineSegment StartX=-120.266 StartY=-35.2585 StartZ=0 EndX=-50.1957 EndY=-35.2585 EndZ=0
    g2: LineSegment StartX=-50.1957 StartY=-35.2585 StartZ=0 EndX=-50.319 EndY=-25.484 EndZ=0
    g3: LineSegment StartX=-50.319 StartY=-25.484 StartZ=0 EndX=-57.7715 EndY=-25.484 EndZ=0
    g4: LineSegment StartX=-65.5367 StartY=-29.5767 StartZ=0 EndX=-109.382 EndY=30.4233 EndZ=0
    g5: LineSegment StartX=-109.382 StartY=30.4233 StartZ=0 EndX=-109.382 EndY=39.9073 EndZ=0
    g6: LineSegment StartX=-109.382 StartY=39.9073 StartZ=0 EndX=-100.312 EndY=39.9073 EndZ=0
    g7: LineSegment StartX=-100.312 StartY=39.9073 StartZ=0 EndX=-100.312 EndY=55.8702 EndZ=0
    g8: LineSegment StartX=-100.312 StartY=55.8702 StartZ=0 EndX=-120.266 EndY=55.8702 EndZ=0
    g9: LineSegment StartX=-65.5367 StartY=-29.5767 StartZ=0 EndX=-57.7715 EndY=-29.5767 EndZ=0
    g10: LineSegment StartX=-57.7715 StartY=-29.5767 StartZ=0 EndX=-57.7715 EndY=-25.484 EndZ=0
  constraints (20):
    c: Vertical(g0)
    c: Coincident(g0,g1)
    c: Horizontal(g1)
    c: Coincident(g1,g2)
    c: Coincident(g2,g3)
    c: Coincident(g4,g5)
    c: Vertical(g5)
    c: Coincident(g5,g6)
    c: Horizontal(g6)
    c: Coincident(g6,g7)
    c: Vertical(g7)
    c: Coincident(g7,g8)
    c: Coincident(g8,g0)
    c: Horizontal(g8)
    c: DistanceY(g4) = 60
    c: Coincident(g9,g4)
    c: Horizontal(g9)
    c: Coincident(g10,g9)
    c: Coincident(g10,g3)
    c: Horizontal(g3)
FEATURE [PartDesign::Pad] Pad008
  Length = 130
  MirroredExtent = false
  Placement = pos=(-1.15663,146.081,200.7) rot=(1,0,0;1.5708rad)
  Sketch = -> Sketch009
FEATURE [Part::Cut] Cut036
  Base = -> Pad008
  Placement = pos=(0.470886,-81.3035,-10.7339) rot=(0,0,1;0rad)
  Tool = -> Box001
FEATURE [Sketcher::SketchObject] Sketch010
  sketch-geometry (4):
    g0: LineSegment StartX=-125.009 StartY=156.743 StartZ=0 EndX=-50.0091 EndY=156.743 EndZ=0
    g1: LineSegment StartX=-50.0091 StartY=156.743 StartZ=0 EndX=-50.0091 EndY=36.7431 EndZ=0
    g2: LineSegment StartX=-50.0091 StartY=36.7431 StartZ=0 EndX=-125.009 EndY=36.7431 EndZ=0
    g3: LineSegment StartX=-125.009 StartY=36.7431 StartZ=0 EndX=-125.009 EndY=156.743 EndZ=0
  constraints (10):
    c: Coincident(g0,g1)
    c: Coincident(g1,g2)
    c: Coincident(g2,g3)
    c: Coincident(g3,g0)
    c: Horizontal(g0)
    c: Horizontal(g2)
    c: Vertical(g1)
    c: Vertical(g3)
    c: DistanceY(g3) = 120
    c: DistanceX(g0) = 75
FEATURE [PartDesign::Pad] Pad009
  Length = 10
  MirroredExtent = false
  Sketch = -> Sketch010
FEATURE [Part::Box] Box002
  Height = 10
  Length = 55
  Placement = pos=(-115,45.8,7.5) rot=(0,0,1;0rad)
  Width = 100
FEATURE [Part::Cut] Cut037  label="display"
  Base = -> Pad009
  Placement = pos=(-34.7923,-97.0035,121.476) rot=(0,1,0;0.928855rad)
  Tool = -> Box002
FEATURE [Part::Box] Box003
  Height = 23
  Length = 23
  Placement = pos=(28.3401,28.6705,-9.64305) rot=(0,0,1;0rad)
  Width = 12
FEATURE [Part::Box] Box004
  Height = 1.7
  Length = 32
  Placement = pos=(24.15,28.6705,7.9668) rot=(0,0,1;0rad)
  Width = 12
FEATURE [Part::Cylinder] Cylinder032
  Angle = 360
  Height = 10
  Placement = pos=(53.8219,34.6,2.58368) rot=(0,0,1;0rad)
  Radius = 1
FEATURE [Part::Cylinder] Cylinder034
  Angle = 360
  Height = 10
  Placement = pos=(26.1112,34.5,1.79316) rot=(0,0,1;0rad)
  Radius = 1
FEATURE [Part::MultiFuse] Fusion003
  Shapes = -> [Box004,Box003]
FEATURE [Part::Cut] Cut038
  Base = -> Fusion003
  Tool = -> Cylinder034
FEATURE [Part::Cut] Cut039
  Base = -> Cut038
  Tool = -> Cylinder032
FEATURE [Part::Cylinder] Cylinder035
  Angle = 360
  Height = 10
  Placement = pos=(41.2515,34.4472,6.56) rot=(0,0,1;0rad)
  Radius = 2
FEATURE [Part::Cylinder] Cylinder036
  Angle = 360
  Height = 10
  Placement = pos=(34.4857,34.67,6.56) rot=(0,0,1;0rad)
  Radius = 6
FEATURE [Part::Box] Box005
  Height = 1.5
  Length = 37
  Width = 4.5
FEATURE [Part::Box] Box006
  Height = 1.5
  Length = 17
  Placement = pos=(20.2342,-6.49055,0) rot=(0,0,1;1.5708rad)
  Width = 4.5
FEATURE [Part::MultiFuse] Fusion004
  Placement = pos=(16.4876,32.0839,17.56) rot=(0,0,1;0rad)
  Shapes = -> [Box006,Box005]
FEATURE [Part::Cylinder] Cylinder037
  Angle = 360
  Height = 10
  Placement = pos=(34.5,34.5,10.7594) rot=(0,0,1;0rad)
  Radius = 2
FEATURE [Part::MultiFuse] Fusion005
  Placement = pos=(-49,17.44,105.53) rot=(0.57735,0.57735,-0.57735;2.0944rad)
  Shapes = -> [Cylinder035,Cylinder036,Cut039]
FEATURE [Part::MultiFuse] Fusion006
  Placement = pos=(-48.6,17.44,105.53) rot=(0.57735,0.57735,-0.57735;2.0944rad)
  Shapes = -> [Fusion004,Cylinder037]
FEATURE [Sketcher::SketchObject] Sketch011
  sketch-geometry (12):
    g0: LineSegment StartX=-95.0946 StartY=32.3618 StartZ=0 EndX=-60.0946 EndY=32.3618 EndZ=0
    g1: LineSegment StartX=-59.724 StartY=-12.6382 StartZ=0 EndX=-95.0946 EndY=-12.6382 EndZ=0
    g2: LineSegment StartX=-95.0946 StartY=-12.6382 StartZ=0 EndX=-95.0946 EndY=32.3618 EndZ=0
    g3: LineSegment StartX=-60.0946 StartY=15.2279 StartZ=0 EndX=-29.8289 EndY=15.2279 EndZ=0
    g4: LineSegment StartX=-29.8289 StartY=15.2279 StartZ=0 EndX=-29.8289 EndY=5.22794 EndZ=0
    g5: LineSegment StartX=-29.8289 StartY=5.22794 StartZ=0 EndX=-59.724 EndY=5.22794 EndZ=0
    g6: LineSegment StartX=-59.724 StartY=-12.6382 StartZ=0 EndX=-59.724 EndY=5.22794 EndZ=0
    g7: LineSegment StartX=-60.0946 StartY=15.2279 StartZ=0 EndX=-60.0946 EndY=32.3618 EndZ=0
    g8: LineSegment StartX=-82.1826 StartY=15.2164 StartZ=0 EndX=-72.1826 EndY=15.2164 EndZ=0
    g9: LineSegment StartX=-72.1826 StartY=15.2164 StartZ=0 EndX=-72.1826 EndY=5.21644 EndZ=0
    g10: LineSegment StartX=-72.1826 StartY=5.21644 StartZ=0 EndX=-82.1826 EndY=5.21644 EndZ=0
    g11: LineSegment StartX=-82.1826 StartY=5.21644 StartZ=0 EndX=-82.1826 EndY=15.2164 EndZ=0
  constraints (29):
    c: Coincident(g1,g2)
    c: Coincident(g2,g0)
    c: Horizontal(g0)
    c: Horizontal(g1)
    c: Vertical(g2)
    c: Coincident(g3,g4)
    c: Coincident(g4,g5)
    c: Horizontal(g3)
    c: Horizontal(g5)
    c: Vertical(g4)
    c: Coincident(g6,g1)
    c: Coincident(g6,g5)
    c: Vertical(g6)
    c: Coincident(g7,g3)
    c: Coincident(g7,g0)
    c: Vertical(g7)
    c: DistanceY(g4) = -10
    c: Coincident(g8,g9)
    c: Coincident(g9,g10)
    c: Coincident(g10,g11)
    c: Coincident(g11,g8)
    c: Horizontal(g8)
    c: Horizontal(g10)
    c: Vertical(g9)
    c: Vertical(g11)
    c: DistanceY(g2) = 45
    c: DistanceX(g0) = 35
    c: DistanceY(g9) = -10
    c: DistanceX(g8) = 10
FEATURE [PartDesign::Pad] Pad010  label="camera_Pad"
  Length = 4
  MirroredExtent = false
  Placement = pos=(-16.3,-10.67,50) rot=(0,1,0;1.5708rad)
  Sketch = -> Sketch011
FEATURE [App::DocumentObjectGroup] Group009  label="micro_servo"
  Group = -> [Fusion006,Fusion005,Pad010]
FEATURE [Part::Feature] RaspBerry
  Placement = pos=(-12.8029,-1.75778,11.0436) rot=(1,0,0;1.5708rad)
  shape: bbox 85.6 x 53.98 x 1.35 mm, 6 faces (baked)
FEATURE [Part::Feature] RaspBerry001
  Placement = pos=(-55.5029,-21.2478,13.6186) rot=(0.57735,-0.57735,-0.57735;2.0944rad)
  shape: bbox 5.461 x 7.999 x 2.949 mm, 809 faces (baked)
FEATURE [Part::Feature] RaspBerry002
  Placement = pos=(-50.8029,-21.2478,13.6186) rot=(0.57735,-0.57735,-0.57735;2.0944rad)
  shape: bbox 3.937 x 6.982 x 2.155 mm, 206 faces (baked)
FEATURE [Part::Feature] RaspBerry003 .. RaspBerry007  x5 (patterned run collapsed; names and placements below)
  shape: bbox 4 x 0.37 x 1.716 mm, 43 faces (baked)
  placements: all 5 at pos=(-50.8029,-21.2478,13.6186) rot=(0.57735,-0.57735,-0.57735;2.0944rad)
FEATURE [Part::Feature] RaspBerry008
  Placement = pos=(-11.3429,-29.2478,15.6986) rot=(1,0,0;1.5708rad)
  shape: bbox 15 x 12 x 8.275 mm, 506 faces (baked)
FEATURE [Part::Feature] RaspBerry009
  Placement = pos=(31.4971,-18.8103,18.9976) rot=(0.57735,0.57735,0.57735;2.0944rad)
  shape: bbox 20.57 x 17.91 x 14.48 mm, 219 faces (baked)
FEATURE [Part::Feature] RaspBerry010
  Placement = pos=(-55.0129,-0.297781,11.0436) rot=(0.57735,0.57735,-0.57735;4.18879rad)
  shape: bbox 3 x 0.7 x 1.3 mm, 115 faces (baked)
FEATURE [Part::Feature] RaspBerry011
  Placement = pos=(-55.0129,-0.297781,11.0436) rot=(0.57735,0.57735,-0.57735;4.18879rad)
  shape: bbox 32.12 x 24.12 x 2.1 mm, 97 faces (baked)
FEATURE [Part::Feature] RaspBerry012
  Placement = pos=(-55.0129,-0.297781,11.0436) rot=(0.57735,0.57735,-0.57735;4.18879rad)
  shape: bbox 4.8 x 1.9 x 0.1 mm, 6 faces (baked)
FEATURE [Part::Feature] RaspBerry013
  Placement = pos=(-55.0129,-0.297781,11.0436) rot=(0.57735,0.57735,-0.57735;4.18879rad)
  shape: bbox 4.8 x 1.9 x 0.1 mm, 6 faces (baked)
FEATURE [Part::Feature] RaspBerry014
  Placement = pos=(-55.0129,-0.297781,11.0436) rot=(0.57735,0.57735,-0.57735;4.18879rad)
  shape: bbox 5.9 x 1.9 x 0.1 mm, 6 faces (baked)
FEATURE [Part::Feature] RaspBerry015
  Placement = pos=(-55.0129,-0.297781,11.0436) rot=(0.57735,0.57735,-0.57735;4.18879rad)
  shape: bbox 5.9 x 1.9 x 0.1 mm, 6 faces (baked)
FEATURE [Part::Feature] RaspBerry016
  Placement = pos=(-55.0129,-0.297781,11.0436) rot=(0.57735,0.57735,-0.57735;4.18879rad)
  shape: bbox 4.8 x 1.9 x 0.1 mm, 6 faces (baked)
FEATURE [Part::Feature] RaspBerry017
  Placement = pos=(-55.0129,-0.297781,11.0436) rot=(0.57735,0.57735,-0.57735;4.18879rad)
  shape: bbox 4.8 x 1.9 x 0.1 mm, 6 faces (baked)
FEATURE [Part::Feature] RaspBerry018
  Placement = pos=(-55.0129,-0.297781,11.0436) rot=(0.57735,0.57735,-0.57735;4.18879rad)
  shape: bbox 4.8 x 3.6 x 0.1 mm, 10 faces (baked)
FEATURE [Part::Feature] RaspBerry019
  Placement = pos=(-55.0129,-0.297781,11.0436) rot=(0.57735,0.57735,-0.57735;4.18879rad)
  shape: bbox 6.819 x 1.9 x 0.1 mm, 9 faces (baked)
FEATURE [Part::Feature] RaspBerry020
  Placement = pos=(9.36709,22.2322,12.3936) rot=(0.57735,-0.57735,-0.57735;2.0944rad)
  shape: bbox 12 x 15 x 10.79 mm, 46 faces (baked)
FEATURE [Part::Feature] RaspBerry021 .. RaspBerry024  x4 (patterned run collapsed; names and placements below)
  shape: bbox 1.145 x 2 x 7.071 mm, 28 faces (baked)
  placements: all 4 at pos=(9.36709,22.2322,12.3936) rot=(0.57735,-0.57735,-0.57735;2.0944rad)
FEATURE [Part::Feature] RaspBerry025
  Placement = pos=(9.36709,22.2322,12.3936) rot=(0.57735,-0.57735,-0.57735;2.0944rad)
  shape: bbox 0.5 x 1.364 x 4.133 mm, 25 faces (baked)
FEATURE [Part::Feature] RaspBerry026
  Placement = pos=(26.4971,1.80222,17.6636) rot=(0.57735,0.57735,0.57735;2.0944rad)
  shape: bbox 17.1 x 13.1 x 15.62 mm, 56 faces (baked)
FEATURE [Part::Feature] RaspBerry027
  Placement = pos=(-8.00671,22.7322,12.3936) rot=(0,0.707107,0.707107;3.14159rad)
  shape: bbox 10.01 x 19.51 x 16.99 mm, 72 faces (baked)
FEATURE [Part::Feature] RaspBerry028
  Placement = pos=(-15.6029,-2.76778,12.3936) rot=(0,0,1;0rad)
  shape: bbox 12 x 12 x 1.4 mm, 6 faces (baked)
FEATURE [Part::Feature] RaspBerry029 .. RaspBerry036  x8 (patterned run collapsed; names and placements below)
  shape: bbox 2.54 x 2.54 x 12.19 mm, 32 faces (baked)
  placements: 8 in arithmetic series — first pos=(-1.27291,14.9622,12.3936) rot=(0,0,1;0rad), step (0,-2.5,0), last pos=(-1.27291,-2.53778,12.3936) rot=(0,0,1;0rad)
FEATURE [Part::Feature] RaspBerry037 .. RaspBerry048  x12 (patterned run collapsed; names and placements below)
  shape: bbox 5.08 x 5.08 x 12.19 mm, 116 faces (baked)
  placements: 12 in arithmetic series — first pos=(-53.3329,20.4222,12.3936) rot=(0,0,1;0rad), step (2.5,0,0), last pos=(-25.8329,20.4222,12.3936) rot=(0,0,1;0rad)
FEATURE [Part::Feature] RaspBerry049
  Placement = pos=(-37.8129,-0.197781,10.9436) rot=(-0.57735,-0.57735,0.57735;2.0944rad)
  shape: bbox 18.89 x 28 x 3.8 mm, 190 faces (baked)
FEATURE [Part::Feature] RaspBerry050
  Placement = pos=(-42.3029,-21.6478,12.3936) rot=(1,0,0;1.5708rad)
  shape: bbox 6.819 x 6.819 x 7.7 mm, 13 faces (baked)
FEATURE [Part::Feature] RaspBerry051
  Placement = pos=(5.53377,-6.74778,12.3936) rot=(0.57735,0.57735,0.57735;2.0944rad)
  shape: bbox 2.6 x 22 x 5.9 mm, 15 faces (baked)
FEATURE [Part::Feature] RaspBerry052
  Placement = pos=(-45.1029,-13.7678,12.3936) rot=(0.57735,-0.57735,-0.57735;2.0944rad)
  shape: bbox 2.6 x 22 x 5.9 mm, 15 faces (baked)
FEATURE [App::DocumentObjectGroup] Group010  label="RPi"
  Group = -> [RaspBerry,RaspBerry002,RaspBerry004,RaspBerry006,RaspBerry008,RaspBerry010,RaspBerry012,RaspBerry014,RaspBerry016,RaspBerry018,RaspBerry020,RaspBerry022,RaspBerry024,RaspBerry026,RaspBerry028,RaspBerry030,RaspBerry032,RaspBerry034,RaspBerry036,RaspBerry038,RaspBerry040,RaspBerry042,RaspBerry044,RaspBerry046,RaspBerry048,RaspBerry050,RaspBerry052,RaspBerry005,RaspBerry009,RaspBerry013,RaspBerry017,+22 more]
FEATURE [Mesh::Feature] rpi_arduino_robot
  Placement = pos=(-14,-4.5,22) rot=(0,0,1;0rad)
